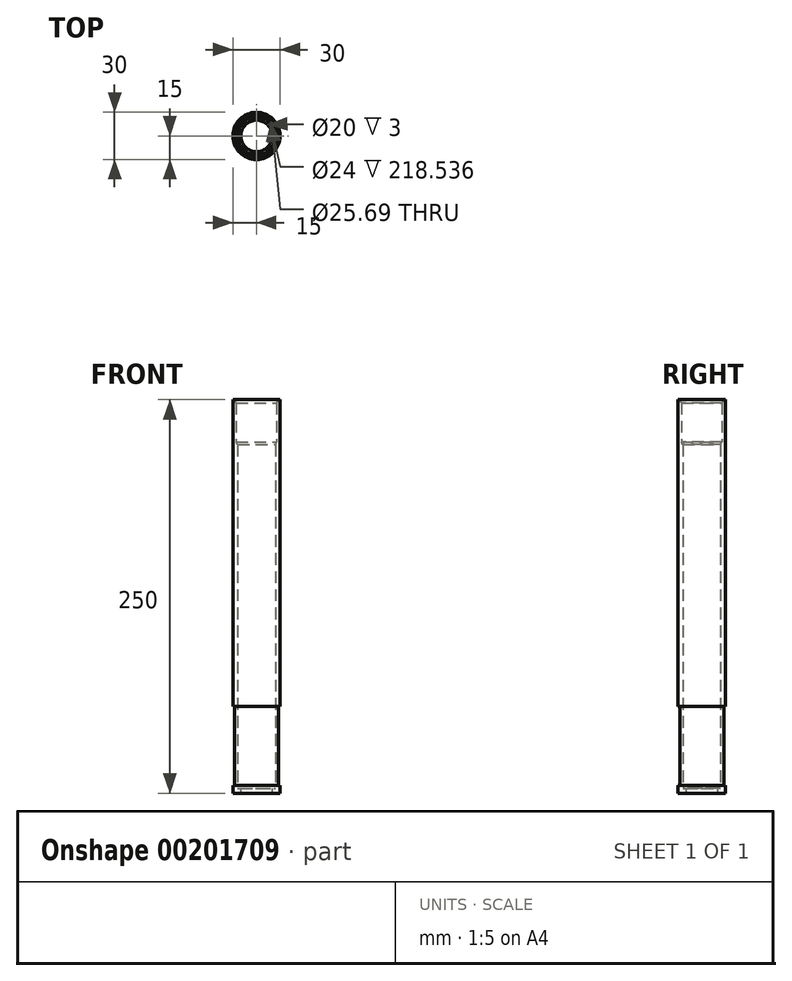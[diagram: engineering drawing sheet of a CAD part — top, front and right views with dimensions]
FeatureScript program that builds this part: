
annotation { "Feature Type Name" : "Feature", "Feature Type Description" : "" }
export const myFeature = defineFeature(function(context is Context, id is Id, definition is map)
    precondition{}
    {
        {
            var Q0;
            Q0=qCreatedBy(makeId("Front.planeOp"),FACE);
            var sketch = newSketch(context, id + "F0", { "sketchPlane" : qUnion([Q0])});
            skLineSegment(sketch, "E0", {"start": v(0, 0) * mm, "end": v(0, 519.9) * mm, "construction": true});
            skLineSegment(sketch, "E1", {"start": v(0, 0) * mm, "end": v(-15, 0) * mm});
            skLineSegment(sketch, "E2", {"start": v(-15, 0) * mm, "end": v(-15, 5) * mm});
            skLineSegment(sketch, "E3", {"start": v(-15, 5) * mm, "end": v(-14, 5) * mm});
            skLineSegment(sketch, "E4", {"start": v(-14, 5) * mm, "end": v(-14, 55) * mm});
            skLineSegment(sketch, "E5", {"start": v(-14, 55) * mm, "end": v(-15, 55) * mm});
            skLineSegment(sketch, "E6", {"start": v(-15, 55) * mm, "end": v(-15, 250) * mm});
            skLineSegment(sketch, "E7", {"start": v(-15, 250) * mm, "end": v(-14, 250) * mm});
            skLineSegment(sketch, "E8", {"start": v(-14, 250) * mm, "end": v(-12.85, 248) * mm});
            skLineSegment(sketch, "E9", {"start": v(-12.85, 248) * mm, "end": v(-12.85, 223) * mm});
            skLineSegment(sketch, "E10", {"start": v(-12.85, 223) * mm, "end": v(-12, 221.54) * mm});
            skLineSegment(sketch, "E11", {"start": v(-12, 221.54) * mm, "end": v(-12, 3) * mm});
            skLineSegment(sketch, "E12", {"start": v(-12, 3) * mm, "end": v(-10, 3) * mm});
            skLineSegment(sketch, "E13", {"start": v(-10, 3) * mm, "end": v(-10, 0) * mm});
            skSolve(sketch);
        }
        {
            var Q0;
            {var subQ0=sQuery(id+"F0.wireOp",EDGE,"E2");Q0=makeQuery(id+"F0.imprint","IMPRINT",FACE,{"disambiguationData":[TD([[makeQuery(id+"F0.imprint","IMPRINT",EDGE,{"derivedFrom":subQ0}),-1.0]])]});}
            var Q1;
            Q1=sQuery(id+"F0.wireOp",EDGE,"E0");
            revolve(context, id + "F1", {"entities" : qUnion([Q0]), "axis" : qUnion([Q1]), "revolveType" : RevolveType.FULL});
        }
    });
